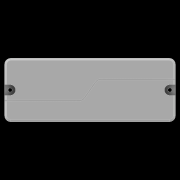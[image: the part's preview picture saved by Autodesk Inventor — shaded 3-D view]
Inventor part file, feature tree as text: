
AUTODESK INVENTOR PART (.ipt)
format: ipt  version: 2020 (Build 240168000, 168)  size: 179,712 bytes
history: native  units: in
note: dims shown in document units (in); Inventor stores cm internally (conversion verified against a paired STEP export)
features: extrude x4, other x1, fillet x1, chamfer x1
ambient origin geometry x8: Origin, YZ Plane, XZ Plane, XY Plane, X Axis, Y Axis, Z Axis, Center Point
bodies: Solid1 (feature_tree)
feature tree (7):
  other  "FishmanModern8"
  extrude  "FishmanModern8Feature"  Depth=4.009in
  fillet  "FishmanModern8FilletsFeature"  Radius=1.492in
  extrude  "FishmanModern8IndentFeature"  Depth=0.1in
  extrude  "FishmanModern8MountsFeature"  Depth=3.75in
  extrude  "FishmanModern8CountersinksFeature"  Depth=1.875in
  chamfer  "FishmanModern8ChamferFeature"  Distance=1.875in
